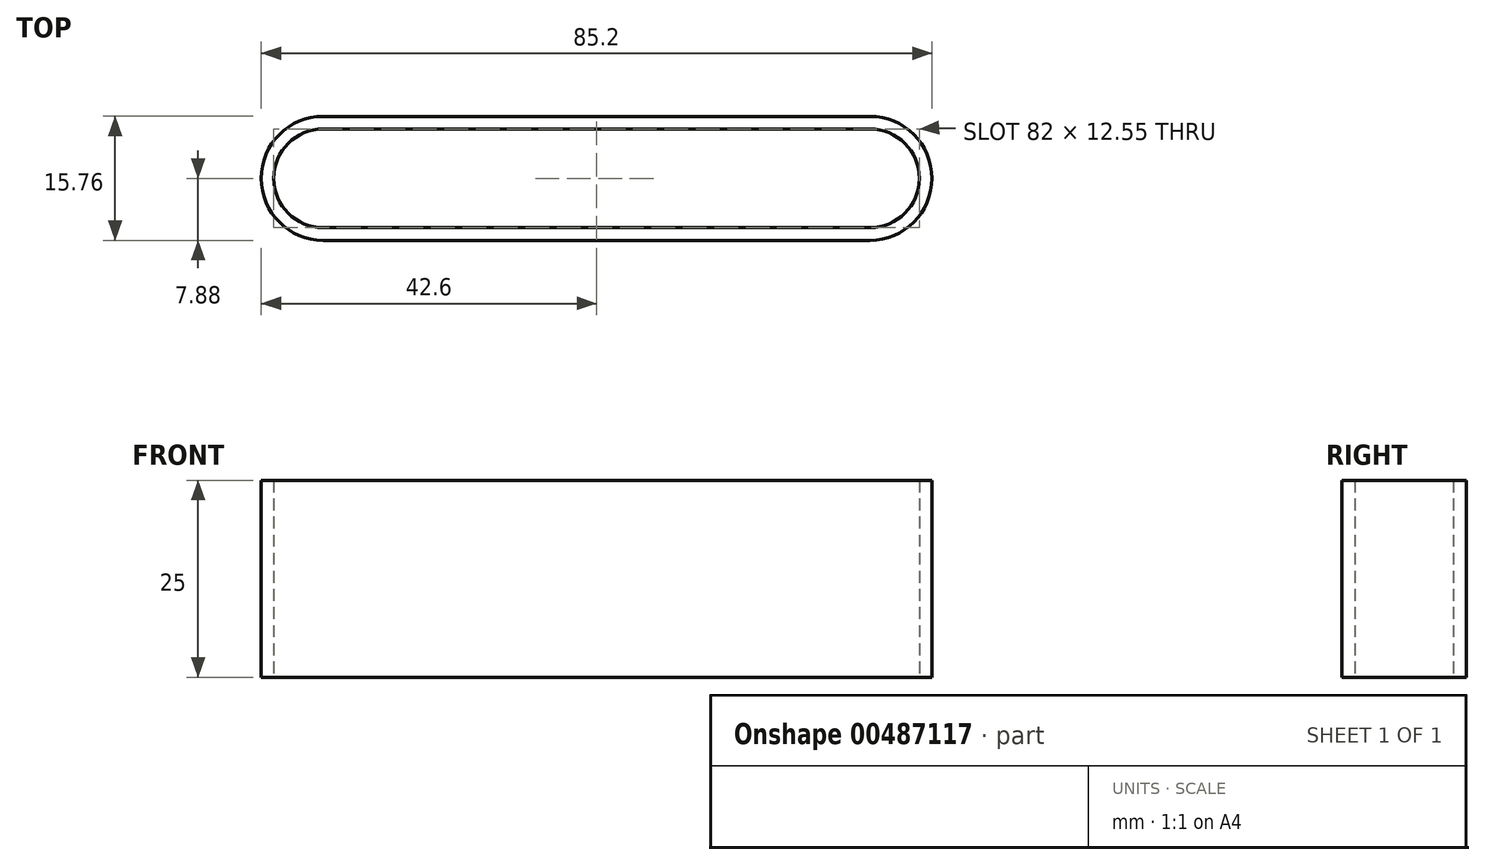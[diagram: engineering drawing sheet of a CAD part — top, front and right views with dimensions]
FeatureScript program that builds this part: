
annotation { "Feature Type Name" : "Feature", "Feature Type Description" : "" }
export const myFeature = defineFeature(function(context is Context, id is Id, definition is map)
    precondition{}
    {
        {
            var Q0;
            Q0=qCreatedBy(makeId("Top.planeOp"),FACE);
            var sketch = newSketch(context, id + "F0", { "sketchPlane" : qUnion([Q0])});
            skLineSegment(sketch, "E0.bottom", {"start": v(34.73, 6.28) * mm, "end": v(-34.73, 6.28) * mm});
            skLineSegment(sketch, "E0.top", {"start": v(34.73, -6.28) * mm, "end": v(-34.73, -6.28) * mm});
            skLineSegment(sketch, "E0.left", {"start": v(41, 0) * mm, "end": v(41, 0) * mm});
            skLineSegment(sketch, "E0.right", {"start": v(-41, 0) * mm, "end": v(-41, 0) * mm});
            skPoint(sketch, "E0.middle", {"position": v(0, 0) * mm});
            skPoint(sketch, "E1.visualSharp", {"position": v(-41, 6.28) * mm});
            skArc(sketch, "E1.filletArc", {"start": v(-34.73, 6.28) * mm, "mid": v(-39.16, 4.44) * mm, "end": v(-41, 0) * mm});
            skPoint(sketch, "E2.visualSharp", {"position": v(-41, -6.28) * mm});
            skArc(sketch, "E2.filletArc", {"start": v(-41, 0) * mm, "mid": v(-39.16, -4.44) * mm, "end": v(-34.73, -6.28) * mm});
            skPoint(sketch, "E3.visualSharp", {"position": v(41, -6.28) * mm});
            skArc(sketch, "E3.filletArc", {"start": v(34.73, -6.28) * mm, "mid": v(39.16, -4.44) * mm, "end": v(41, 0) * mm});
            skPoint(sketch, "E4.visualSharp", {"position": v(41, 6.28) * mm});
            skArc(sketch, "E4.filletArc", {"start": v(41, 0) * mm, "mid": v(39.16, 4.44) * mm, "end": v(34.73, 6.28) * mm});
            skArc(sketch, "E5.0", {"start": v(34.73, -7.87) * mm, "mid": v(40.3, -5.57) * mm, "end": v(42.6, 0) * mm});
            skLineSegment(sketch, "E5.1", {"start": v(34.73, 7.87) * mm, "end": v(-34.73, 7.87) * mm});
            skArc(sketch, "E5.2", {"start": v(-34.73, 7.87) * mm, "mid": v(-40.3, 5.57) * mm, "end": v(-42.6, 0) * mm});
            skArc(sketch, "E5.3", {"start": v(42.6, 0) * mm, "mid": v(40.3, 5.57) * mm, "end": v(34.73, 7.87) * mm});
            skArc(sketch, "E5.4", {"start": v(-42.6, 0) * mm, "mid": v(-40.3, -5.57) * mm, "end": v(-34.73, -7.87) * mm});
            skLineSegment(sketch, "E5.5", {"start": v(34.73, -7.87) * mm, "end": v(-34.73, -7.87) * mm});
            skSolve(sketch);
        }
        {
            var Q0;
            Q0=makeQuery(id+"F0.imprint","IMPRINT",FACE,{"disambiguationData":[TD([[makeQuery(id+"F0.imprint","IMPRINT",EDGE,{"derivedFrom":sQuery(id+"F0.wireOp",EDGE,"E0.bottom")}),-1.0]])]});
            extrude(context, id + "F1", {"entities" : qUnion([Q0]), "depth" : 25 * mm});
        }
    });
